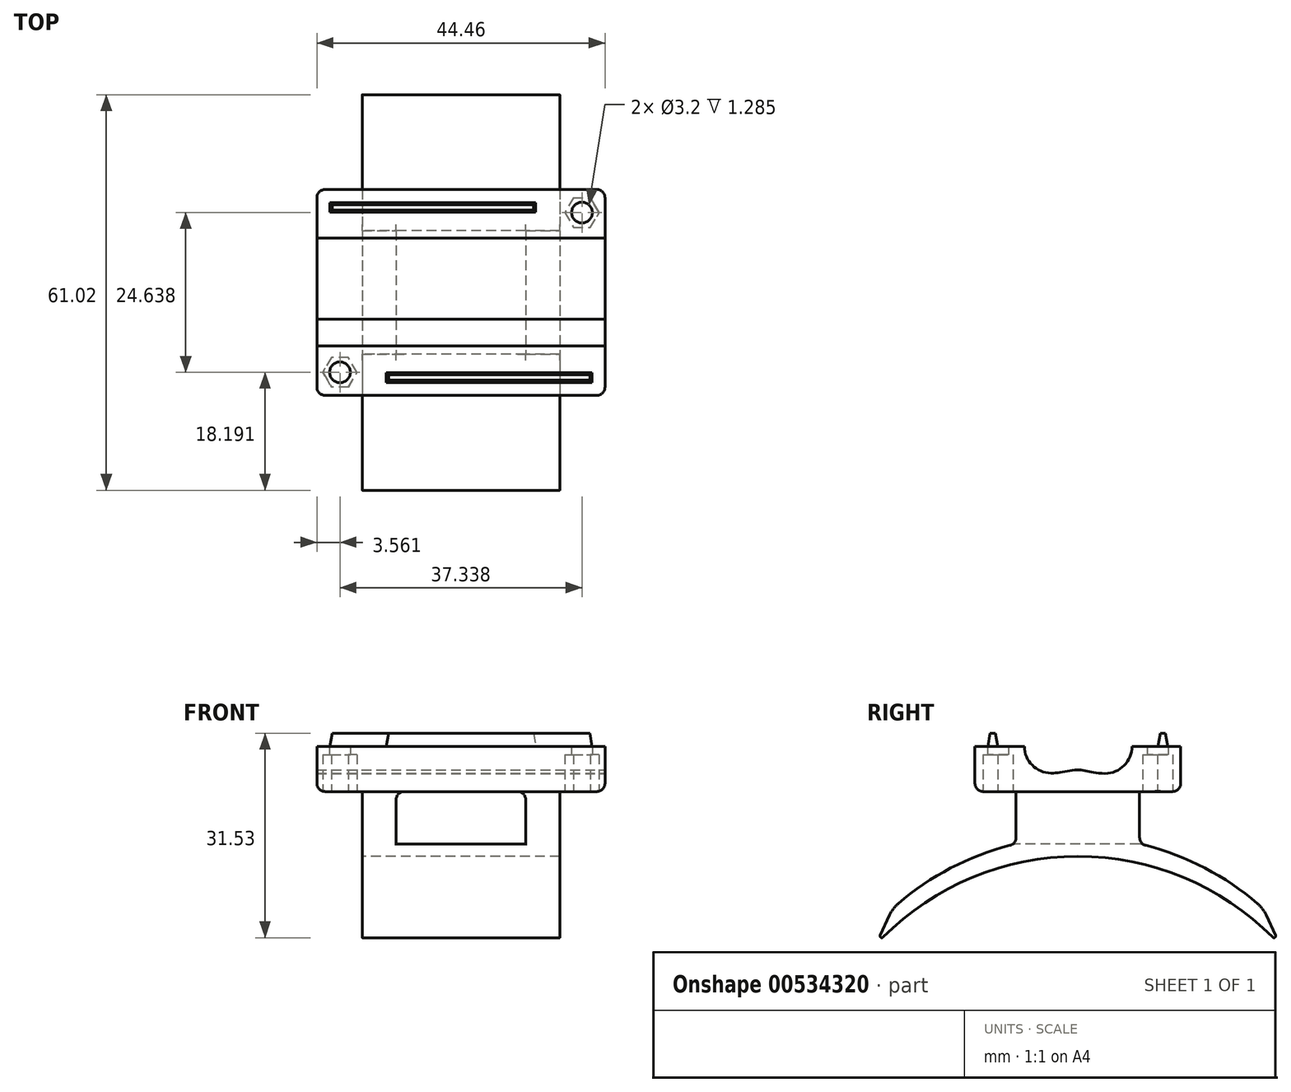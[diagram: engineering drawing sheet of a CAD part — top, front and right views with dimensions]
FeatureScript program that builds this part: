
annotation { "Feature Type Name" : "Feature", "Feature Type Description" : "" }
export const myFeature = defineFeature(function(context is Context, id is Id, definition is map)
    precondition{}
    {
        {
            var Q0;
            Q0=qCreatedBy(makeId("Top.planeOp"),FACE);
            var sketch = newSketch(context, id + "F0", { "sketchPlane" : qUnion([Q0])});
            skLineSegment(sketch, "E0.bottom", {"start": v(-38.1, 0) * mm, "end": v(38.1, 0) * mm});
            skLineSegment(sketch, "E0.top", {"start": v(-38.1, -4.13) * mm, "end": v(38.1, -4.13) * mm});
            skLineSegment(sketch, "E0.left", {"start": v(-38.1, 0) * mm, "end": v(-38.1, -4.13) * mm});
            skLineSegment(sketch, "E0.right", {"start": v(38.1, 0) * mm, "end": v(38.1, -4.13) * mm});
            skLineSegment(sketch, "E1.top", {"start": v(-38.1, 4.2) * mm, "end": v(38.1, 4.2) * mm});
            skLineSegment(sketch, "E1.left", {"start": v(-38.1, 0) * mm, "end": v(-38.1, 4.2) * mm});
            skLineSegment(sketch, "E1.right", {"start": v(38.1, 0) * mm, "end": v(38.1, 4.2) * mm});
            skLineSegment(sketch, "E2.MirrorCS", {"start": v(38.1, 8.38) * mm, "end": v(38.1, 4.2) * mm});
            skLineSegment(sketch, "E3.MirrorCS", {"start": v(-38.1, 8.38) * mm, "end": v(38.1, 8.38) * mm});
            skLineSegment(sketch, "E4.MirrorCS", {"start": v(-38.1, 8.38) * mm, "end": v(-38.1, 4.2) * mm});
            skLineSegment(sketch, "E5.MirrorCS", {"start": v(38.1, -8.25) * mm, "end": v(38.1, -4.12) * mm});
            skLineSegment(sketch, "E6.MirrorCS", {"start": v(-38.1, -8.25) * mm, "end": v(38.1, -8.25) * mm});
            skLineSegment(sketch, "E7.MirrorCS", {"start": v(-38.1, -8.25) * mm, "end": v(-38.1, -4.12) * mm});
            skSolve(sketch);
        }
        {
            var Q0;
            Q0=qCreatedBy(makeId("Top.planeOp"),FACE);
            var sketch = newSketch(context, id + "F1", { "sketchPlane" : qUnion([Q0])});
            skLineSegment(sketch, "E8.bottom", {"start": v(-22.23, 15.88) * mm, "end": v(22.23, 15.88) * mm});
            skLineSegment(sketch, "E8.top", {"start": v(-22.23, -15.88) * mm, "end": v(22.23, -15.88) * mm});
            skLineSegment(sketch, "E8.left", {"start": v(-22.23, 15.87) * mm, "end": v(-22.23, -15.88) * mm});
            skLineSegment(sketch, "E8.right", {"start": v(22.23, 15.88) * mm, "end": v(22.23, -15.87) * mm});
            skSolve(sketch);
        }
        {
            var Q0;
            Q0 = qSketchRegion(id + "F1", true);
            extrude(context, id + "F2", {"entities" : qUnion([Q0]), "oppositeDirection" : true, "depth" : 7 * mm, "offsetDistance" : 25.4 * mm});
        }
        {
            var Q0;
            Q0=makeQuery(id+"F2.opExtrude","SWEPT_FACE",FACE,{"disambiguationData":[OSD([sQuery(id+"F1.wireOp",EDGE,"E8.right")])]});
            var sketch = newSketch(context, id + "F3", { "sketchPlane" : qUnion([Q0])});
            skLineSegment(sketch, "E9.0", {"start": v(-8.25, 0) * mm, "end": v(-4.12, 0) * mm});
            skLineSegment(sketch, "E10.0", {"start": v(8.38, 0) * mm, "end": v(4.2, 0) * mm});
            skArc(sketch, "E11", {"start": v(-4.13, 4.13) * mm, "mid": v(-8.25, 0) * mm, "end": v(-4.12, -4.13) * mm});
            skArc(sketch, "E12", {"start": v(4.2, -4.2) * mm, "mid": v(8.38, 0) * mm, "end": v(4.2, 4.2) * mm});
            skFitSpline(sketch, "E13", {"points": [v(-4.12, 4.13) * mm, v(0, 3.54) * mm, v(4.2, 4.2) * mm], "startDerivative": vector(10.24, -0.07) * mm, "endDerivative": vector(9.95, 0.46) * mm});
            skFitSpline(sketch, "E14", {"points": [v(-4.12, -4.13) * mm, v(0, -3.63) * mm, v(4.2, -4.2) * mm], "startDerivative": vector(7.18, -0.46) * mm, "endDerivative": vector(12.23, 0.06) * mm});
            skSolve(sketch);
        }
        {
            var Q0;
            Q0 = qSketchRegion(id + "F3", true);
            var Q1;
            Q1=makeQuery(id+"F2.opExtrude","SWEPT_FACE",FACE,{"disambiguationData":[OSD([sQuery(id+"F1.wireOp",EDGE,"E8.left")])]});
            extrude(context, id + "F4", {"entities" : qUnion([Q0]), "operationType" : NewBodyOperationType.REMOVE, "endBound" : BoundingType.UP_TO_SURFACE, "oppositeDirection" : true, "depth" : 25.4 * mm, "endBoundEntityFace" : qUnion([Q1]), "offsetDistance" : 25.4 * mm});
        }
        {
            var Q0;
            Q0=qCreatedBy(makeId("Right.planeOp"),FACE);
            var sketch = newSketch(context, id + "F5", { "sketchPlane" : qUnion([Q0])});
            skArc(sketch, "E15", {"start": v(31.11, -30.53) * mm, "mid": v(0, -16.99) * mm, "end": v(-31.11, -30.53) * mm});
            skArc(sketch, "E16", {"start": v(28.58, -25.03) * mm, "mid": v(0, -13.99) * mm, "end": v(-28.57, -25.03) * mm});
            skLineSegment(sketch, "E17.0", {"start": v(15.88, -6.99) * mm, "end": v(-15.87, -6.99) * mm});
            skLineSegment(sketch, "E18", {"start": v(9.52, -15.07) * mm, "end": v(9.52, -6.99) * mm});
            skLineSegment(sketch, "E19", {"start": v(9.52, -6.99) * mm, "end": v(-9.52, -6.99) * mm});
            skLineSegment(sketch, "E20", {"start": v(-9.52, -6.99) * mm, "end": v(-9.52, -15.07) * mm});
            skLineSegment(sketch, "E21", {"start": v(-31.11, -30.53) * mm, "end": v(-28.57, -25.03) * mm});
            skLineSegment(sketch, "E22", {"start": v(28.58, -25.03) * mm, "end": v(31.12, -30.53) * mm});
            skSolve(sketch);
        }
        {
            var Q0;
            Q0 = qSketchRegion(id + "F5", true);
            extrude(context, id + "F6", {"entities" : qUnion([Q0]), "operationType" : NewBodyOperationType.ADD, "depth" : 15.24 * mm, "offsetDistance" : 25.4 * mm, "hasSecondDirection" : true, "secondDirectionOppositeDirection" : true, "secondDirectionDepth" : 15.24 * mm});
        }
        {
            var Q0;
            Q0=makeQuery(id+"F6.opExtrude","SWEPT_FACE",FACE,{"disambiguationData":[OSD([sQuery(id+"F5.wireOp",EDGE,"E20")])]});
            var sketch = newSketch(context, id + "F7", { "sketchPlane" : qUnion([Q0])});
            skLineSegment(sketch, "E23.bottom", {"start": v(-10, -6.99) * mm, "end": v(10, -6.99) * mm});
            skLineSegment(sketch, "E23.top", {"start": v(-10, -15.07) * mm, "end": v(10, -15.07) * mm});
            skLineSegment(sketch, "E23.left", {"start": v(-10, -6.99) * mm, "end": v(-10, -15.07) * mm});
            skLineSegment(sketch, "E23.right", {"start": v(10, -6.98) * mm, "end": v(10, -15.07) * mm});
            skSolve(sketch);
        }
        {
            var Q0;
            Q0 = qSketchRegion(id + "F7", true);
            extrude(context, id + "F8", {"entities" : qUnion([Q0]), "operationType" : NewBodyOperationType.REMOVE, "oppositeDirection" : true, "depth" : 25.4 * mm, "offsetDistance" : 25.4 * mm});
        }
        {
            var Q0;
            Q0=makeQuery(id+"F8.boolean.opBoolean","MERGE",FACE,{"derivedFrom":[makeQuery(id+"F2.opExtrude","CAP_FACE",FACE,{"disambiguationData":[OSD([sQuery(id+"F1.wireOp",EDGE,"E8.bottom"),sQuery(id+"F1.wireOp",EDGE,"E8.top"),sQuery(id+"F1.wireOp",EDGE,"E8.left"),sQuery(id+"F1.wireOp",EDGE,"E8.right")])],"isStart":false}),makeQuery(id+"F8.opExtrude","SWEPT_FACE",FACE,{"disambiguationData":[OSD([sQuery(id+"F7.wireOp",EDGE,"E23.bottom")])]})]});
            var sketch = newSketch(context, id + "F9", { "sketchPlane" : qUnion([Q0])});
            skCircle(sketch, "E24", {"center": v(-18.67, 12.32) * mm, "radius": 1.6 * mm});
            skCircle(sketch, "E25", {"center": v(18.67, -12.32) * mm, "radius": 1.6 * mm});
            skSolve(sketch);
        }
        {
            var Q0;
            Q0 = qSketchRegion(id + "F9", true);
            extrude(context, id + "F10", {"entities" : qUnion([Q0]), "operationType" : NewBodyOperationType.REMOVE, "oppositeDirection" : true, "depth" : 25.4 * mm, "offsetDistance" : 25.4 * mm});
        }
        {
            var Q0;
            Q0=makeQuery(id+"F8.boolean.opBoolean","MERGE",FACE,{"derivedFrom":[makeQuery(id+"F2.opExtrude","CAP_FACE",FACE,{"disambiguationData":[OSD([sQuery(id+"F1.wireOp",EDGE,"E8.bottom"),sQuery(id+"F1.wireOp",EDGE,"E8.top"),sQuery(id+"F1.wireOp",EDGE,"E8.left"),sQuery(id+"F1.wireOp",EDGE,"E8.right")])],"isStart":false}),makeQuery(id+"F8.opExtrude","SWEPT_FACE",FACE,{"disambiguationData":[OSD([sQuery(id+"F7.wireOp",EDGE,"E23.bottom")])]})]});
            var sketch = newSketch(context, id + "F11", { "sketchPlane" : qUnion([Q0])});
            skCircle(sketch, "E26.0", {"center": v(-18.67, 12.32) * mm, "radius": 1.6 * mm});
            skCircle(sketch, "E27.0", {"center": v(18.67, -12.32) * mm, "radius": 1.6 * mm});
            skCircle(sketch, "E28.cCircle", {"center": v(-18.67, 12.32) * mm, "radius": 2.65 * mm, "construction": true});
            skLineSegment(sketch, "E28.0", {"start": v(-16.02, 12.32) * mm, "end": v(-17.34, 10.02) * mm});
            skLineSegment(sketch, "E28.1", {"start": v(-17.34, 10.02) * mm, "end": v(-20, 10.02) * mm});
            skLineSegment(sketch, "E28.2", {"start": v(-20, 10.02) * mm, "end": v(-21.32, 12.32) * mm});
            skLineSegment(sketch, "E28.3", {"start": v(-21.32, 12.32) * mm, "end": v(-20, 14.61) * mm});
            skLineSegment(sketch, "E28.4", {"start": v(-20, 14.61) * mm, "end": v(-17.34, 14.61) * mm});
            skLineSegment(sketch, "E28.5", {"start": v(-17.34, 14.61) * mm, "end": v(-16.02, 12.32) * mm});
            skCircle(sketch, "E29.cCircle", {"center": v(18.67, -12.32) * mm, "radius": 2.65 * mm, "construction": true});
            skLineSegment(sketch, "E29.0", {"start": v(21.32, -12.32) * mm, "end": v(20, -14.61) * mm});
            skLineSegment(sketch, "E29.1", {"start": v(20, -14.61) * mm, "end": v(17.34, -14.61) * mm});
            skLineSegment(sketch, "E29.2", {"start": v(17.34, -14.61) * mm, "end": v(16.02, -12.32) * mm});
            skLineSegment(sketch, "E29.3", {"start": v(16.02, -12.32) * mm, "end": v(17.34, -10.02) * mm});
            skLineSegment(sketch, "E29.4", {"start": v(17.34, -10.02) * mm, "end": v(20, -10.02) * mm});
            skLineSegment(sketch, "E29.5", {"start": v(20, -10.02) * mm, "end": v(21.32, -12.32) * mm});
            skSolve(sketch);
        }
        {
            var Q0;
            Q0 = qSketchRegion(id + "F11", true);
            extrude(context, id + "F12", {"entities" : qUnion([Q0]), "operationType" : NewBodyOperationType.REMOVE, "oppositeDirection" : true, "depth" : 5.7 * mm, "offsetDistance" : 25.4 * mm});
        }
        {
            var Q0;
            {var subQ0=sQuery(id+"F1.wireOp",EDGE,"E8.bottom");var subQ1=sQuery(id+"F1.wireOp",EDGE,"E8.right");var subQ2=sQuery(id+"F1.wireOp",EDGE,"E8.left");Q0=makeQuery(id+"F4.boolean.opBoolean","SPLIT",FACE,{"disambiguationData":[TD([makeQuery(id+"F2.opExtrude","SWEPT_FACE",FACE,{"disambiguationData":[OSD([subQ0])]})])],"derivedFrom":makeQuery(id+"F2.opExtrude","CAP_FACE",FACE,{"disambiguationData":[OSD([subQ0,sQuery(id+"F1.wireOp",EDGE,"E8.top"),subQ2,subQ1])],"isStart":true})});}
            var sketch = newSketch(context, id + "F13", { "sketchPlane" : qUnion([Q0])});
            skLineSegment(sketch, "E30.bottom", {"start": v(-20.23, 13.88) * mm, "end": v(11.53, 13.88) * mm});
            skLineSegment(sketch, "E30.top", {"start": v(-20.23, 12.37) * mm, "end": v(11.53, 12.37) * mm});
            skLineSegment(sketch, "E30.left", {"start": v(-20.23, 13.88) * mm, "end": v(-20.23, 12.37) * mm});
            skLineSegment(sketch, "E30.right", {"start": v(11.53, 13.88) * mm, "end": v(11.53, 12.37) * mm});
            skLineSegment(sketch, "E31.bottom", {"start": v(20.23, -13.88) * mm, "end": v(-11.53, -13.88) * mm});
            skLineSegment(sketch, "E31.top", {"start": v(20.23, -12.38) * mm, "end": v(-11.53, -12.38) * mm});
            skLineSegment(sketch, "E31.left", {"start": v(20.23, -13.88) * mm, "end": v(20.23, -12.38) * mm});
            skLineSegment(sketch, "E31.right", {"start": v(-11.53, -13.88) * mm, "end": v(-11.53, -12.38) * mm});
            skSolve(sketch);
        }
        {
            var Q0;
            Q0 = qSketchRegion(id + "F13", true);
            extrude(context, id + "F14", {"entities" : qUnion([Q0]), "operationType" : NewBodyOperationType.ADD, "depth" : 2 * mm, "offsetDistance" : 25.4 * mm, "hasDraft" : true, "draftAngle" : 10 * degree, "draftPullDirection" : true});
        }
        {
            var Q0;
            Q0=makeQuery(id+"F6.opExtrude","SWEPT_EDGE",EDGE,{"disambiguationData":[OSD([sQuery(id+"F5.wireOp",EDGE,"E15"),sQuery(id+"F5.wireOp",EDGE,"E22")])]});
            var Q1;
            Q1=makeQuery(id+"F6.opExtrude","SWEPT_EDGE",EDGE,{"disambiguationData":[OSD([sQuery(id+"F5.wireOp",EDGE,"E15"),sQuery(id+"F5.wireOp",EDGE,"E21")])]});
            fillet(context, id + "F15", {"entities" : qUnion([Q0, Q1]), "radius" : 0.25 * mm, "tangentPropagation" : true, "allowEdgeOverflow" : false});
        }
        {
            var Q0;
            Q0=makeQuery(id+"F6.opExtrude","SWEPT_EDGE",EDGE,{"disambiguationData":[OSD([sQuery(id+"F5.wireOp",EDGE,"E16"),sQuery(id+"F5.wireOp",EDGE,"E22")])]});
            var Q1;
            Q1=makeQuery(id+"F6.opExtrude","SWEPT_EDGE",EDGE,{"disambiguationData":[OSD([sQuery(id+"F5.wireOp",EDGE,"E16"),sQuery(id+"F5.wireOp",EDGE,"E21")])]});
            fillet(context, id + "F16", {"entities" : qUnion([Q0, Q1]), "radius" : 5.08 * mm, "tangentPropagation" : true, "allowEdgeOverflow" : false});
        }
        {
            var Q0;
            {var subQ1=sQuery(id+"F5.wireOp",EDGE,"E16");var subQ2=sQuery(id+"F5.wireOp",EDGE,"E20");Q0=makeQuery(id+"F8.boolean.opBoolean","SPLIT",EDGE,{"disambiguationData":[TD([makeQuery(id+"F8.opExtrude","SWEPT_FACE",FACE,{"disambiguationData":[OSD([sQuery(id+"F7.wireOp",EDGE,"E23.right")])]})])],"derivedFrom":makeQuery(id+"F6.opExtrude","SWEPT_EDGE",EDGE,{"disambiguationData":[OSD([subQ1,subQ2])]})});}
            var Q1;
            {var subQ0=sQuery(id+"F5.wireOp",EDGE,"E20");var subQ2=sQuery(id+"F5.wireOp",EDGE,"E16");Q1=makeQuery(id+"F8.boolean.opBoolean","SPLIT",EDGE,{"disambiguationData":[TD([makeQuery(id+"F8.opExtrude","SWEPT_FACE",FACE,{"disambiguationData":[OSD([sQuery(id+"F7.wireOp",EDGE,"E23.left")])]})])],"derivedFrom":makeQuery(id+"F6.opExtrude","SWEPT_EDGE",EDGE,{"disambiguationData":[OSD([subQ2,subQ0])]})});}
            var Q2;
            {var subQ0=sQuery(id+"F5.wireOp",EDGE,"E18");var subQ1=makeQuery(id+"F6.opExtrude","SWEPT_FACE",FACE,{"disambiguationData":[OSD([subQ0])]});var subQ2=sQuery(id+"F5.wireOp",EDGE,"E22");var subQ3=sQuery(id+"F5.wireOp",EDGE,"E16");var subQ4=makeQuery(id+"F6.opExtrude","SWEPT_FACE",FACE,{"disambiguationData":[OSD([subQ3]),TDD([makeQuery(id+"F5.imprint","IMPRINT",EDGE,{"disambiguationData":[TD([[makeQuery(id+"F5.imprint","INTERSECT",VERTEX,{"derivedFrom":[subQ3,subQ2]}),-1.0]])],"derivedFrom":subQ3})])]});Q2=makeQuery(id+"F8.boolean.opBoolean","SPLIT",EDGE,{"disambiguationData":[topologyDisambiguationEdgeConnected([subQ4,subQ1]),TD([makeQuery(id+"F8.opExtrude","SWEPT_FACE",FACE,{"disambiguationData":[OSD([sQuery(id+"F7.wireOp",EDGE,"E23.right")])]})])],"derivedFrom":makeQuery(id+"F6.opExtrude","SWEPT_EDGE",EDGE,{"disambiguationData":[OSD([subQ3,subQ0])]})});}
            var Q3;
            {var subQ0=sQuery(id+"F5.wireOp",EDGE,"E18");var subQ1=makeQuery(id+"F6.opExtrude","SWEPT_FACE",FACE,{"disambiguationData":[OSD([subQ0])]});var subQ2=sQuery(id+"F5.wireOp",EDGE,"E22");var subQ3=sQuery(id+"F5.wireOp",EDGE,"E16");var subQ4=makeQuery(id+"F6.opExtrude","SWEPT_FACE",FACE,{"disambiguationData":[OSD([subQ3]),TDD([makeQuery(id+"F5.imprint","IMPRINT",EDGE,{"disambiguationData":[TD([[makeQuery(id+"F5.imprint","INTERSECT",VERTEX,{"derivedFrom":[subQ3,subQ2]}),-1.0]])],"derivedFrom":subQ3})])]});Q3=makeQuery(id+"F8.boolean.opBoolean","SPLIT",EDGE,{"disambiguationData":[topologyDisambiguationEdgeConnected([subQ4,subQ1]),TD([makeQuery(id+"F8.opExtrude","SWEPT_FACE",FACE,{"disambiguationData":[OSD([sQuery(id+"F7.wireOp",EDGE,"E23.left")])]})])],"derivedFrom":makeQuery(id+"F6.opExtrude","SWEPT_EDGE",EDGE,{"disambiguationData":[OSD([subQ3,subQ0])]})});}
            fillet(context, id + "F17", {"entities" : qUnion([Q0, Q1, Q2, Q3]), "radius" : 1.27 * mm, "tangentPropagation" : true, "allowEdgeOverflow" : false});
        }
        {
            var Q0;
            {var subQ0=sQuery(id+"F5.wireOp",EDGE,"E18");var subQ1=sQuery(id+"F5.wireOp",EDGE,"E19");Q0=makeQuery(id+"F8.boolean.opBoolean","SPLIT",EDGE,{"disambiguationData":[TD([makeQuery(id+"F8.opExtrude","SWEPT_FACE",FACE,{"disambiguationData":[OSD([sQuery(id+"F7.wireOp",EDGE,"E23.right")])]})])],"derivedFrom":makeQuery(id+"F6.opExtrude","SWEPT_EDGE",EDGE,{"disambiguationData":[OSD([subQ0,subQ1])]})});}
            var Q1;
            Q1=makeQuery(id+"F6.opExtrude","CAP_EDGE",EDGE,{"disambiguationData":[OSD([sQuery(id+"F5.wireOp",EDGE,"E19")])],"isStart":false});
            var Q2;
            {var subQ0=sQuery(id+"F5.wireOp",EDGE,"E20");var subQ1=sQuery(id+"F5.wireOp",EDGE,"E19");Q2=makeQuery(id+"F8.boolean.opBoolean","SPLIT",EDGE,{"disambiguationData":[TD([makeQuery(id+"F8.opExtrude","SWEPT_FACE",FACE,{"disambiguationData":[OSD([sQuery(id+"F7.wireOp",EDGE,"E23.right")])]})])],"derivedFrom":makeQuery(id+"F6.opExtrude","SWEPT_EDGE",EDGE,{"disambiguationData":[OSD([subQ1,subQ0])]})});}
            var Q3;
            Q3=makeQuery(id+"F8.boolean.opBoolean","COPY",EDGE,{"derivedFrom":makeQuery(id+"F8.opExtrude","SWEPT_EDGE",EDGE,{"disambiguationData":[OSD([sQuery(id+"F5.wireOp",EDGE,"E19"),sQuery(id+"F5.wireOp",EDGE,"E20"),sQuery(id+"F7.wireOp",EDGE,"E23.bottom"),sQuery(id+"F7.wireOp",EDGE,"E23.right")])]})});
            var Q4;
            {var subQ0=sQuery(id+"F5.wireOp",EDGE,"E20");var subQ1=sQuery(id+"F5.wireOp",EDGE,"E19");Q4=makeQuery(id+"F8.boolean.opBoolean","SPLIT",EDGE,{"disambiguationData":[TD([makeQuery(id+"F8.opExtrude","SWEPT_FACE",FACE,{"disambiguationData":[OSD([sQuery(id+"F7.wireOp",EDGE,"E23.left")])]})])],"derivedFrom":makeQuery(id+"F6.opExtrude","SWEPT_EDGE",EDGE,{"disambiguationData":[OSD([subQ1,subQ0])]})});}
            var Q5;
            Q5=makeQuery(id+"F6.opExtrude","CAP_EDGE",EDGE,{"disambiguationData":[OSD([sQuery(id+"F5.wireOp",EDGE,"E19")])],"isStart":true});
            var Q6;
            Q6=makeQuery(id+"F8.boolean.opBoolean","COPY",EDGE,{"derivedFrom":makeQuery(id+"F8.opExtrude","SWEPT_EDGE",EDGE,{"disambiguationData":[OSD([sQuery(id+"F5.wireOp",EDGE,"E19"),sQuery(id+"F5.wireOp",EDGE,"E20"),sQuery(id+"F7.wireOp",EDGE,"E23.bottom"),sQuery(id+"F7.wireOp",EDGE,"E23.left")])]})});
            var Q7;
            {var subQ0=sQuery(id+"F5.wireOp",EDGE,"E18");var subQ1=sQuery(id+"F5.wireOp",EDGE,"E19");Q7=makeQuery(id+"F8.boolean.opBoolean","SPLIT",EDGE,{"disambiguationData":[TD([makeQuery(id+"F8.opExtrude","SWEPT_FACE",FACE,{"disambiguationData":[OSD([sQuery(id+"F7.wireOp",EDGE,"E23.left")])]})])],"derivedFrom":makeQuery(id+"F6.opExtrude","SWEPT_EDGE",EDGE,{"disambiguationData":[OSD([subQ0,subQ1])]})});}
            fillet(context, id + "F18", {"entities" : qUnion([Q0, Q1, Q2, Q3, Q4, Q5, Q6, Q7]), "radius" : 1.27 * mm, "tangentPropagation" : true, "allowEdgeOverflow" : false});
        }
        {
            var Q0;
            Q0=makeQuery(id+"F2.opExtrude","SWEPT_EDGE",EDGE,{"disambiguationData":[OSD([sQuery(id+"F1.wireOp",EDGE,"E8.top"),sQuery(id+"F1.wireOp",EDGE,"E8.left")])]});
            var Q1;
            Q1=makeQuery(id+"F2.opExtrude","CAP_EDGE",EDGE,{"disambiguationData":[OSD([sQuery(id+"F1.wireOp",EDGE,"E8.left")])],"isStart":false});
            var Q2;
            Q2=makeQuery(id+"F2.opExtrude","CAP_EDGE",EDGE,{"disambiguationData":[OSD([sQuery(id+"F1.wireOp",EDGE,"E8.top")])],"isStart":false});
            var Q3;
            Q3=makeQuery(id+"F2.opExtrude","SWEPT_EDGE",EDGE,{"disambiguationData":[OSD([sQuery(id+"F1.wireOp",EDGE,"E8.top"),sQuery(id+"F1.wireOp",EDGE,"E8.right")])]});
            var Q4;
            Q4=makeQuery(id+"F2.opExtrude","CAP_EDGE",EDGE,{"disambiguationData":[OSD([sQuery(id+"F1.wireOp",EDGE,"E8.right")])],"isStart":false});
            var Q5;
            Q5=makeQuery(id+"F2.opExtrude","SWEPT_EDGE",EDGE,{"disambiguationData":[OSD([sQuery(id+"F1.wireOp",EDGE,"E8.bottom"),sQuery(id+"F1.wireOp",EDGE,"E8.right")])]});
            var Q6;
            Q6=makeQuery(id+"F2.opExtrude","CAP_EDGE",EDGE,{"disambiguationData":[OSD([sQuery(id+"F1.wireOp",EDGE,"E8.bottom")])],"isStart":false});
            var Q7;
            Q7=makeQuery(id+"F2.opExtrude","SWEPT_EDGE",EDGE,{"disambiguationData":[OSD([sQuery(id+"F1.wireOp",EDGE,"E8.bottom"),sQuery(id+"F1.wireOp",EDGE,"E8.left")])]});
            fillet(context, id + "F19", {"entities" : qUnion([Q0, Q1, Q2, Q3, Q4, Q5, Q6, Q7]), "radius" : 1.27 * mm, "tangentPropagation" : true, "allowEdgeOverflow" : false});
        }
    });
